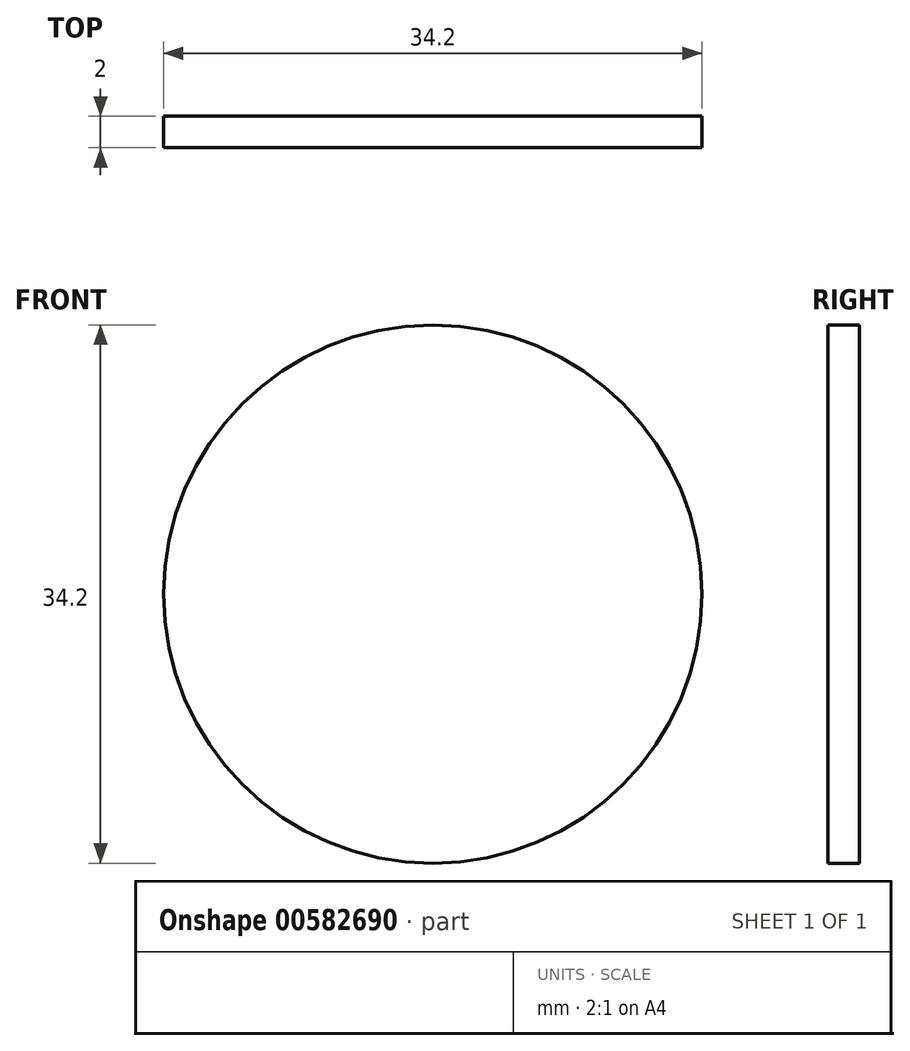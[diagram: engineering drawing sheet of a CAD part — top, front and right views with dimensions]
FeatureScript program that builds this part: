
annotation { "Feature Type Name" : "Feature", "Feature Type Description" : "" }
export const myFeature = defineFeature(function(context is Context, id is Id, definition is map)
    precondition{}
    {
        {
            var Q0;
            Q0=qCreatedBy(makeId("Front.planeOp"),FACE);
            var sketch = newSketch(context, id + "F0", { "sketchPlane" : qUnion([Q0])});
            skCircle(sketch, "E0", {"center": v(0, 0) * mm, "radius": 17.1 * mm});
            skSolve(sketch);
        }
        {
            var Q0;
            Q0=makeQuery(id+"F0.imprint","IMPRINT",FACE,{"disambiguationData":[TD([[makeQuery(id+"F0.imprint","IMPRINT",EDGE,{"derivedFrom":sQuery(id+"F0.wireOp",EDGE,"E0")}),1.0]])]});
            extrude(context, id + "F1", {"entities" : qUnion([Q0]), "depth" : 2 * mm, "offsetDistance" : 25 * mm});
        }
    });
